FCSTD DOCUMENT  (FreeCAD 0.18R4 (GitTag))
Label: winding2
License: All rights reserved
LicenseURL: http://en.wikipedia.org/wiki/All_rights_reserved
objects: Sketcher::SketchObject×5, PartDesign::Body×2, Spreadsheet::Sheet×1
note: 7 computed .brp shape members not serialized (recipe doc carries the construction recipe); baked Part::Feature solids carry a one-line shape summary decoded from their .brp

FEATURE [Spreadsheet::Sheet] Spreadsheet  label="Variables"
  cells = A2=slotNumber; B2(slotNumber)=6; A3=outerDiameter; B3(outerDiameter)=50.15; A4=innerDiameter; B4(innerDiameter)=8; A5=stackLength; B5(stackLength)=26; A6=stackingFactor; B6(stackingFactor)=0.95; A7=cuttingThickness; B7(cuttingThickness)=0.1; A8=skewAngle; B8(skewAngle)=0; A9=segmentAngle; B9(segmentAngle)==360 / slotNumber; A10=tipHeightReduction; B10(tipHeightReduction)=50; A11=toothThickness; B11(toothThickness)=3; A12=yokeThickness; B12(yokeThickness)=2.8; A13=tipHeight; B13(tipHeight)=0.8; A14=tipAngle; B14(tipAngle)=95; A15=openingLeft; B15(openingLeft)=1; A16=openingRight; B16(openingRight)=1; A17=slotIsolation; B17(slotIsolation)=0.5; A18=windingAngle; B18(windingAngle)=35; A19=heightRatio; B19(heightRatio)=45; A20=roundingRadii; B20(roundingRadii)=0.2; A21=coilAxialHeight; B21(coilAxialHeight)=15
FEATURE [Sketcher::SketchObject] Sketch003  label="StatorSegment"
  MapMode = 5
  Support = -> [XY_Plane]
  expr: Constraints[71] = Variables.innerDiameter / 2
  expr: Constraints[26] = Variables.toothThickness / 2
  expr: Constraints[9] = Variables.segmentAngle
  expr: Constraints[27] = Variables.innerDiameter / 2 + Variables.yokeThickness
  expr: Constraints[35] = Variables.roundingRadii
  expr: Constraints[61] = Variables.tipHeight
  expr: Constraints[23] = Variables.tipAngle
  expr: Constraints[16] = Variables.tipHeight * (1 - Variables.tipHeightReduction / 100)
  expr: Constraints[12] = Variables.openingLeft
  expr: Constraints[72] = Variables.segmentAngle / 2
  expr: Constraints[5] = Variables.outerDiameter
  sketch-geometry (29):
    g0: ArcOfCircle [constr] CenterX=0 CenterY=0 CenterZ=0 NormalX=0 NormalY=0 NormalZ=1 AngleXU=0 Radius=25.075 StartAngle=-1.15e-14 EndAngle=1.0472
    g1: LineSegment [constr] StartX=0 StartY=0 StartZ=0 EndX=12.5375 EndY=21.7156 EndZ=0
    g2: LineSegment [constr] StartX=0 StartY=0 StartZ=0 EndX=25.075 EndY=-2.877e-13 EndZ=0
    g3: LineSegment [constr] StartX=0 StartY=0 StartZ=0 EndX=21.7156 EndY=12.5375 EndZ=0
    g4: LineSegment [constr] StartX=0.999801 StartY=25.0551 StartZ=0 EndX=21.1984 EndY=13.3934 EndZ=0
    g5: LineSegment [constr] StartX=21.1984 StartY=13.3934 StartZ=0 EndX=20.5958 EndY=13.0454 EndZ=0
    g6: LineSegment [constr] StartX=20.5056 StartY=12.9934 StartZ=0 EndX=20.852 EndY=13.1934 EndZ=0
    g7: ArcOfCircle CenterX=1.54226 CenterY=2.67128 CenterZ=0 NormalX=0 NormalY=0 NormalZ=1 AngleXU=0 Radius=21.9905 StartAngle=0.498928 EndAngle=1.0472
    g8: LineSegment StartX=20.4112 StartY=13.0374 StartZ=0 EndX=11.7908 EndY=17.0572 EndZ=0
    g9: LineSegment StartX=11.5331 StartY=16.9759 StartZ=0 EndX=4.84974 EndY=5.4 EndZ=0
    g10: LineSegment StartX=4.84974 StartY=5.2 StartZ=0 EndX=5.88897 EndY=3.4 EndZ=0
    g11: LineSegment [constr] StartX=4.84974 StartY=5.4 StartZ=0 EndX=3.5507 EndY=6.15 EndZ=0
    g12: LineSegment StartX=5.88897 StartY=3.4 StartZ=0 EndX=6.9282 EndY=1.6 EndZ=0
    g13: LineSegment StartX=7.10141 StartY=1.5 StartZ=0 EndX=20.4681 EndY=1.5 EndZ=0
    g14: LineSegment StartX=20.6673 StartY=1.68257 StartZ=0 EndX=21.4963 EndY=11.158 EndZ=0
    g15: LineSegment StartX=21.5956 StartY=11.3137 StartZ=0 EndX=21.8518 EndY=11.4617 EndZ=0
    g16: ArcOfCircle CenterX=3.08453 CenterY=2.65e-14 CenterZ=0 NormalX=0 NormalY=0 NormalZ=1 AngleXU=0 Radius=21.9905 StartAngle=-1.15e-14 EndAngle=0.548269
    g17: ArcOfCircle CenterX=21.6956 CenterY=11.1405 CenterZ=0 NormalX=0 NormalY=0 NormalZ=1 AngleXU=0 Radius=0.2 StartAngle=2.0944 EndAngle=3.05433
    g18: ArcOfCircle CenterX=20.4681 CenterY=1.7 CenterZ=0 NormalX=0 NormalY=0 NormalZ=1 AngleXU=0 Radius=0.2 StartAngle=4.71239 EndAngle=6.19592
    g19: ArcOfCircle CenterX=7.10141 CenterY=1.7 CenterZ=0 NormalX=0 NormalY=0 NormalZ=1 AngleXU=0 Radius=0.2 StartAngle=3.66519 EndAngle=4.71239
    g20: ArcOfCircle CenterX=11.7063 CenterY=16.8759 CenterZ=0 NormalX=0 NormalY=0 NormalZ=1 AngleXU=0 Radius=0.2 StartAngle=1.13446 EndAngle=2.61799
    g21: ArcOfCircle CenterX=20.4958 CenterY=13.2186 CenterZ=0 NormalX=0 NormalY=0 NormalZ=1 AngleXU=0 Radius=0.2 StartAngle=4.27606 EndAngle=5.23599
    g22: ArcOfCircle CenterX=5.02295 CenterY=5.3 CenterZ=0 NormalX=0 NormalY=0 NormalZ=1 AngleXU=0 Radius=0.2 StartAngle=2.61799 EndAngle=3.66519
    g23: LineSegment [constr] StartX=20.4112 StartY=13.0374 StartZ=0 EndX=20.5056 EndY=12.9934 EndZ=0
    g24: LineSegment [constr] StartX=20.5056 StartY=12.9934 StartZ=0 EndX=20.5958 EndY=13.0454 EndZ=0
    g25: LineSegment StartX=20.5958 StartY=13.0454 StartZ=0 EndX=20.852 EndY=13.1934 EndZ=0
    g26: LineSegment StartX=12.5375 StartY=21.7156 StartZ=0 EndX=2 EndY=3.4641 EndZ=0
    g27: LineSegment StartX=4 StartY=-4.59e-14 StartZ=0 EndX=25.075 EndY=-2.877e-13 EndZ=0
    g28: ArcOfCircle CenterX=0 CenterY=0 CenterZ=0 NormalX=0 NormalY=0 NormalZ=1 AngleXU=0 Radius=4 StartAngle=-1.15e-14 EndAngle=1.0472
  constraints (73):
    c: Coincident(g0,g-1)
    c: Coincident(g1,g0)
    c: Coincident(g1,g0)
    c: Coincident(g2,g0)
    c: Coincident(g2,g0)
    c: Diameter(g0) = 50.15
    c: Coincident(g3,g0)
    c: PointOnObject(g3,g0)
    c: Symmetric(g0,g0,g3)
    c: Angle(g2,g1) = 1.0472
    c: PointOnObject(g4,g0)
    c: Symmetric(g4,g4,g1)
    c: Distance(g4,g3) = 1
    c: Coincident(g5,g4)
    c: Parallel(g5,g3)
    c: PointOnObject(g6,g5)
    c: Distance(g6) = 0.4
    c: Coincident(g7,g0)
    c: Coincident(g7,g6)
    c: PointOnObject(g7,g1)
    c: PointOnObject(g10,g3)
    c: Perpendicular(g3,g10)
    c: Parallel(g1,g9)
    c: Angle(g9,g8) = 1.65806
    c: PointOnObject(g11,g1)
    c: Perpendicular(g1,g11)
    c: Distance(g11) = 1.5
    c: Distance(g-1,g10) = 6.8
    c: Coincident(g12,g10)
    c: Symmetric(g15,g7,g3)
    c: PointOnObject(g16,g2)
    c: Coincident(g16,g0)
    c: Coincident(g16,g15)
    c: Tangent(g14,g17) = 1.5708
    c: Tangent(g15,g17) = 1.5708
    c: Radius(g17) = 0.2
    c: Tangent(g13,g18) = -1.5708
    c: Tangent(g14,g18) = -1.5708
    c: Tangent(g12,g19) = -1.5708
    c: Tangent(g13,g19) = -1.5708
    c: Tangent(g8,g20) = -1.5708
    c: Tangent(g9,g20) = -1.5708
    c: Tangent(g5,g21) = 1.5708
    c: Tangent(g8,g21) = 1.5708
    c: Tangent(g10,g22) = -1.5708
    c: Tangent(g9,g22) = -1.5708
    c: Coincident(g11,g9)
    c: Equal(g17,g18)
    c: Equal(g19,g17)
    c: Equal(g22,g17)
    c: Equal(g20,g17)
    c: Symmetric(g13,g9,g3)
    c: Symmetric(g14,g8,g3)
    c: Symmetric(g14,g8,g3)
    c: Equal(g21,g17)
    c: Coincident(g23,g8)
    c: Coincident(g24,g23)
    c: Coincident(g24,g5)
    c: Parallel(g23,g8)
    c: Parallel(g24,g5)
    c: Coincident(g6,g23)
    c: Distance(g6,g4) = 0.8
    c: Coincident(g25,g21)
    c: Coincident(g25,g7)
    c: Coincident(g26,g7)
    c: PointOnObject(g26,g1)
    c: PointOnObject(g27,g2)
    c: Coincident(g27,g16)
    c: Coincident(g28,g-1)
    c: Coincident(g28,g26)
    c: Coincident(g28,g27)
    c: Radius(g28) = 4
    c: Angle(g-1,g3) = 0.523599
FEATURE [Sketcher::SketchObject] Sketch007  label="TerminalLeft"
  ExternalGeometry = -> [Sketch003]
  MapMode = 5
  Support = -> [XY_Plane]
  expr: Constraints[40] = Variables.slotIsolation / 2
  expr: Constraints[35] = Variables.windingAngle
  expr: Constraints[31] = 90
  expr: Constraints[21] = Variables.toothThickness / 2 + Variables.slotIsolation
  expr: Constraints[20] = Variables.innerDiameter / 2 + Variables.yokeThickness + Variables.slotIsolation
  expr: Constraints[5] = Variables.slotIsolation / sin(Variables.windingAngle)
  expr: Constraints[2] = (Variables.outerDiameter / 2 - Variables.innerDiameter / 2 - Variables.yokeThickness - Variables.tipHeight) * Variables.heightRatio / 100
  sketch-geometry (20):
    g0: LineSegment [constr] StartX=5.88897 StartY=3.4 StartZ=0 EndX=12.6992 EndY=7.33188 EndZ=0
    g1: LineSegment [constr] StartX=12.6992 StartY=7.33188 StartZ=0 EndX=12.2633 EndY=8.08681 EndZ=0
    g2: LineSegment [constr] StartX=19.8806 StartY=12.731 StartZ=0 EndX=11.8277 EndY=16.4862 EndZ=0
    g3: LineSegment [constr] StartX=11.8277 StartY=16.4862 StartZ=0 EndX=5.36936 EndY=5.3 EndZ=0
    g4: LineSegment [constr] StartX=5.36936 StartY=5.3 StartZ=0 EndX=7.27461 EndY=2 EndZ=0
    g5: LineSegment [constr] StartX=7.27461 StartY=2 StartZ=0 EndX=20.1913 EndY=2 EndZ=0
    g6: LineSegment [constr] StartX=20.1913 StartY=2 StartZ=0 EndX=20.9657 EndY=10.8516 EndZ=0
    g7: LineSegment [constr] StartX=20.9657 StartY=10.8516 StartZ=0 EndX=19.8806 EndY=12.731 EndZ=0
    g8: GeomPoint X=6.32199 Y=3.65 Z=0
    g9: LineSegment [constr] StartX=21.4963 StartY=11.158 StartZ=0 EndX=20.4112 EndY=13.0374 EndZ=0
    g10: LineSegment [constr] StartX=11.8277 StartY=16.4862 StartZ=0 EndX=11.3728 EndY=16.6983 EndZ=0
    g11: LineSegment [constr] StartX=11.8277 StartY=16.4862 StartZ=0 EndX=12.0398 EndY=16.941 EndZ=0
    g12: LineSegment [constr] StartX=7.8484 StartY=9.59383 StartZ=0 EndX=24.1334 EndY=2 EndZ=0
    g13: LineSegment [constr] StartX=7.97388 StartY=9.81116 StartZ=0 EndX=16.9541 EndY=5.6236 EndZ=0
    g14: LineSegment [constr] StartX=16.8485 StartY=5.39703 StartZ=0 EndX=16.9541 EndY=5.6236 EndZ=0
    g15: LineSegment [constr] StartX=16.9541 StartY=5.6236 StartZ=0 EndX=20.4112 EndY=13.0374 EndZ=0
    g16: LineSegment StartX=11.8277 StartY=16.4862 StartZ=0 EndX=20.1991 EndY=12.5825 EndZ=0
    g17: LineSegment StartX=20.1991 StartY=12.5825 StartZ=0 EndX=16.9541 EndY=5.6236 EndZ=0
    g18: LineSegment StartX=16.9541 StartY=5.6236 StartZ=0 EndX=7.97388 EndY=9.81116 EndZ=0
    g19: LineSegment StartX=7.97388 StartY=9.81116 StartZ=0 EndX=11.8277 EndY=16.4862 EndZ=0
  constraints (54):
    c: Coincident(g0,g-6)
    c: Perpendicular(g0,g-5)
    c: Distance(g0) = 7.86375
    c: Coincident(g1,g0)
    c: Parallel(g1,g-5)
    c: Distance(g1) = 0.871723
    c: Coincident(g2,g3)
    c: Coincident(g3,g4)
    c: Coincident(g4,g5)
    c: Horizontal(g5)
    c: Coincident(g5,g6)
    c: Coincident(g6,g7)
    c: Coincident(g7,g2)
    c: Parallel(g2,g-3)
    c: Parallel(g6,g-8)
    c: Parallel(g7,g4)
    c: Symmetric(g4,g3,g0)
    c: Symmetric(g5,g2,g0)
    c: PointOnObject(g8,g4)
    c: PointOnObject(g8,g0)
    c: Distance(g-1,g8) = 7.3
    c: DistanceY(g-1,g4) = 2
    c: Coincident(g9,g-8)
    c: Coincident(g9,g-3)
    c: Equal(g9,g7)
    c: Coincident(g10,g2)
    c: PointOnObject(g10,g-4)
    c: Coincident(g11,g2)
    c: PointOnObject(g11,g-3)
    c: Angle(g11,g10) = 1.5708
    c: Equal(g10,g11)
    c: Angle(g2,g11) = 1.5708
    c: PointOnObject(g12,g3)
    c: PointOnObject(g12,g5)
    c: PointOnObject(g0,g12)
    c: Angle(g4,g12) = 0.610865
    c: PointOnObject(g14,g12)
    c: PointOnObject(g13,g3)
    c: Coincident(g14,g13)
    c: Angle(g13,g14) = 1.5708
    c: Distance(g14) = 0.25
    c: Parallel(g12,g13)
    c: Coincident(g15,g13)
    c: Coincident(g15,g9)
    c: Parallel(g15,g14)
    c: Coincident(g16,g2)
    c: PointOnObject(g16,g15)
    c: Parallel(g16,g2)
    c: Coincident(g17,g16)
    c: Coincident(g17,g13)
    c: Coincident(g18,g17)
    c: Coincident(g18,g13)
    c: Coincident(g19,g18)
    c: Coincident(g19,g16)
FEATURE [Sketcher::SketchObject] Sketch008  label="TerminalRight"
  ExternalGeometry = -> [Sketch003]
  MapMode = 5
  Support = -> [XY_Plane]
  expr: Constraints[52] = Variables.slotIsolation / 2
  expr: Constraints[40] = Variables.slotIsolation / 2
  expr: Constraints[35] = Variables.windingAngle
  expr: Constraints[31] = 90
  expr: Constraints[21] = Variables.toothThickness / 2 + Variables.slotIsolation
  expr: Constraints[20] = Variables.innerDiameter / 2 + Variables.yokeThickness + Variables.slotIsolation
  expr: Constraints[5] = Variables.slotIsolation / sin(Variables.windingAngle)
  expr: Constraints[2] = (Variables.outerDiameter / 2 - Variables.innerDiameter / 2 - Variables.yokeThickness - Variables.tipHeight) * Variables.heightRatio / 100
  sketch-geometry (23):
    g0: LineSegment [constr] StartX=5.88897 StartY=3.4 StartZ=0 EndX=12.6992 EndY=7.33188 EndZ=0
    g1: LineSegment [constr] StartX=12.6992 StartY=7.33188 StartZ=0 EndX=12.2633 EndY=8.08681 EndZ=0
    g2: LineSegment [constr] StartX=19.8806 StartY=12.731 StartZ=0 EndX=11.8277 EndY=16.4862 EndZ=0
    g3: LineSegment [constr] StartX=11.8277 StartY=16.4862 StartZ=0 EndX=5.36936 EndY=5.3 EndZ=0
    g4: LineSegment [constr] StartX=5.36936 StartY=5.3 StartZ=0 EndX=7.27461 EndY=2 EndZ=0
    g5: LineSegment [constr] StartX=7.27461 StartY=2 StartZ=0 EndX=20.1913 EndY=2 EndZ=0
    g6: LineSegment [constr] StartX=20.1913 StartY=2 StartZ=0 EndX=20.9657 EndY=10.8516 EndZ=0
    g7: LineSegment [constr] StartX=20.9657 StartY=10.8516 StartZ=0 EndX=19.8806 EndY=12.731 EndZ=0
    g8: GeomPoint X=6.32199 Y=3.65 Z=0
    g9: LineSegment [constr] StartX=21.4963 StartY=11.158 StartZ=0 EndX=20.4112 EndY=13.0374 EndZ=0
    g10: LineSegment [constr] StartX=11.8277 StartY=16.4862 StartZ=0 EndX=11.3728 EndY=16.6983 EndZ=0
    g11: LineSegment [constr] StartX=11.8277 StartY=16.4862 StartZ=0 EndX=12.0398 EndY=16.941 EndZ=0
    g12: LineSegment [constr] StartX=7.8484 StartY=9.59383 StartZ=0 EndX=24.1334 EndY=2 EndZ=0
    g13: LineSegment [constr] StartX=7.97388 StartY=9.81116 StartZ=0 EndX=16.9541 EndY=5.6236 EndZ=0
    g14: LineSegment [constr] StartX=16.8485 StartY=5.39702 StartZ=0 EndX=16.9541 EndY=5.6236 EndZ=0
    g15: LineSegment [constr] StartX=16.9541 StartY=5.6236 StartZ=0 EndX=20.4112 EndY=13.0374 EndZ=0
    g16: LineSegment [constr] StartX=16.8485 StartY=5.39702 StartZ=0 EndX=15.2644 EndY=2 EndZ=0
    g17: LineSegment StartX=7.72292 StartY=9.3765 StartZ=0 EndX=16.7428 EndY=5.17045 EndZ=0
    g18: LineSegment [constr] StartX=16.7428 StartY=5.17045 StartZ=0 EndX=16.8485 EndY=5.39702 EndZ=0
    g19: LineSegment StartX=7.72292 StartY=9.3765 StartZ=0 EndX=5.36936 EndY=5.3 EndZ=0
    g20: LineSegment StartX=5.36936 StartY=5.3 StartZ=0 EndX=7.27461 EndY=2 EndZ=0
    g21: LineSegment StartX=7.27461 StartY=2 StartZ=0 EndX=15.2644 EndY=2 EndZ=0
    g22: LineSegment StartX=15.2644 StartY=2 StartZ=0 EndX=16.7428 EndY=5.17045 EndZ=0
  constraints (62):
    c: Coincident(g0,g-6)
    c: Perpendicular(g0,g-5)
    c: Distance(g0) = 7.86375
    c: Coincident(g1,g0)
    c: Parallel(g1,g-5)
    c: Distance(g1) = 0.871723
    c: Coincident(g2,g3)
    c: Coincident(g3,g4)
    c: Coincident(g4,g5)
    c: Horizontal(g5)
    c: Coincident(g5,g6)
    c: Coincident(g6,g7)
    c: Coincident(g7,g2)
    c: Parallel(g2,g-3)
    c: Parallel(g6,g-8)
    c: Parallel(g7,g4)
    c: Symmetric(g4,g3,g0)
    c: Symmetric(g5,g2,g0)
    c: PointOnObject(g8,g4)
    c: PointOnObject(g8,g0)
    c: Distance(g-1,g8) = 7.3
    c: DistanceY(g-1,g4) = 2
    c: Coincident(g9,g-8)
    c: Coincident(g9,g-3)
    c: Equal(g9,g7)
    c: Coincident(g10,g2)
    c: PointOnObject(g10,g-4)
    c: Coincident(g11,g2)
    c: PointOnObject(g11,g-3)
    c: Angle(g11,g10) = 1.5708
    c: Equal(g10,g11)
    c: Angle(g2,g11) = 1.5708
    c: PointOnObject(g12,g3)
    c: PointOnObject(g12,g5)
    c: PointOnObject(g0,g12)
    c: Angle(g4,g12) = 0.610865
    c: PointOnObject(g14,g12)
    c: PointOnObject(g13,g3)
    c: Coincident(g14,g13)
    c: Angle(g13,g14) = 1.5708
    c: Distance(g14) = 0.25
    c: Parallel(g12,g13)
    c: Coincident(g15,g13)
    c: Coincident(g15,g9)
    c: Parallel(g15,g14)
    c: Coincident(g16,g14)
    c: PointOnObject(g16,g5)
    c: Parallel(g16,g15)
    c: PointOnObject(g17,g3)
    c: PointOnObject(g17,g16)
    c: Coincident(g18,g17)
    c: Coincident(g18,g14)
    c: Distance(g18) = 0.25
    c: Angle(g18,g17) = 1.5708
    c: Coincident(g19,g17)
    c: Coincident(g19,g3)
    c: Coincident(g20,g19)
    c: Coincident(g20,g4)
    c: Coincident(g21,g20)
    c: Coincident(g21,g16)
    c: Coincident(g22,g21)
    c: Coincident(g22,g17)
FEATURE [PartDesign::Body] Body  label="TopView"
  Group = -> [Sketch003,Sketch007,Sketch008]
  Origin = -> Origin
FEATURE [Sketcher::SketchObject] Sketch  label="StatorSde"
  MapMode = 5
  Support = -> [XY_Plane001]
  expr: Constraints[20] = Variables.stackLength
  expr: Constraints[17] = Variables.innerDiameter
  expr: Constraints[16] = Variables.outerDiameter
  sketch-geometry (8):
    g0: LineSegment StartX=-13 StartY=25.075 StartZ=0 EndX=13 EndY=25.075 EndZ=0
    g1: LineSegment StartX=13 StartY=25.075 StartZ=0 EndX=13 EndY=4 EndZ=0
    g2: LineSegment StartX=13 StartY=4 StartZ=0 EndX=-13 EndY=4 EndZ=0
    g3: LineSegment StartX=-13 StartY=4 StartZ=0 EndX=-13 EndY=25.075 EndZ=0
    g4: LineSegment StartX=-13 StartY=-4 StartZ=0 EndX=13 EndY=-4 EndZ=0
    g5: LineSegment StartX=13 StartY=-4 StartZ=0 EndX=13 EndY=-25.075 EndZ=0
    g6: LineSegment StartX=13 StartY=-25.075 StartZ=0 EndX=-13 EndY=-25.075 EndZ=0
    g7: LineSegment StartX=-13 StartY=-25.075 StartZ=0 EndX=-13 EndY=-4 EndZ=0
  constraints (21):
    c: Coincident(g0,g1)
    c: Coincident(g1,g2)
    c: Coincident(g2,g3)
    c: Coincident(g3,g0)
    c: Horizontal(g0)
    c: Vertical(g1)
    c: Vertical(g3)
    c: Coincident(g4,g5)
    c: Coincident(g5,g6)
    c: Coincident(g6,g7)
    c: Coincident(g7,g4)
    c: Horizontal(g6)
    c: Vertical(g5)
    c: Vertical(g7)
    c: Symmetric(g2,g1,g-2)
    c: Symmetric(g4,g4,g-2)
    c: DistanceY(g6,g0) = 50.15
    c: DistanceY(g4,g2) = 8
    c: Symmetric(g4,g2,g-1)
    c: Equal(g7,g3)
    c: DistanceX(g6,g6) = 26
FEATURE [Sketcher::SketchObject] Sketch009  label="WindingSide"
  ExternalGeometry = -> [Sketch]
  MapMode = 5
  Support = -> [XY_Plane001]
  expr: Constraints[18] = Variables.coilAxialHeight
  expr: Constraints[8] = Variables.coilAxialHeight
  sketch-geometry (12):
    g0: ArcOfEllipse CenterX=-13 CenterY=0 CenterZ=0 NormalX=0 NormalY=0 NormalZ=1 MajorRadius=25.075 MinorRadius=15 AngleXU=1.5708 StartAngle=1e-16 EndAngle=3.14159
    g1: LineSegment [constr] StartX=-13 StartY=25.075 StartZ=0 EndX=-13 EndY=-25.075 EndZ=0
    g2: LineSegment [constr] StartX=-28 StartY=0 StartZ=0 EndX=2 EndY=0 EndZ=0
    g3: GeomPoint X=-13 Y=20.0937 Z=0
    g4: GeomPoint X=-13 Y=-20.0937 Z=0
    g5: LineSegment StartX=-13 StartY=25.075 StartZ=0 EndX=-13 EndY=-25.075 EndZ=0
    g6: ArcOfEllipse CenterX=13 CenterY=0 CenterZ=0 NormalX=0 NormalY=0 NormalZ=1 MajorRadius=25.075 MinorRadius=15 AngleXU=-1.5708 StartAngle=-9.8e-15 EndAngle=3.14159
    g7: LineSegment [constr] StartX=13 StartY=-25.075 StartZ=0 EndX=13 EndY=25.075 EndZ=0
    g8: LineSegment [constr] StartX=28 StartY=0 StartZ=0 EndX=-2 EndY=0 EndZ=0
    g9: GeomPoint X=13 Y=-20.0937 Z=0
    g10: GeomPoint X=13 Y=20.0937 Z=0
    g11: LineSegment StartX=13 StartY=25.075 StartZ=0 EndX=13 EndY=-25.075 EndZ=0
  constraints (18):
    c: InternalAlignment(g1-g4 -> g0) x4
    c: PointOnObject(g0,g-4)
    c: Horizontal(g2)
    c: PointOnObject(g0,g-1)
    c: PointOnObject(g1,g-3)
    c: DistanceX(g2,g0) = 15
    c: Coincident(g0,g-3)
    c: Coincident(g5,g0)
    c: Coincident(g5,g0)
    c: InternalAlignment(g7-g10 -> g6) x4
    c: PointOnObject(g6,g-1)
    c: Coincident(g6,g-6)
    c: DistanceX(g6,g8) = 15
    c: Coincident(g6,g7)
    c: Horizontal(g8)
    c: PointOnObject(g6,g7)
    c: Coincident(g11,g6)
    c: Coincident(g11,g6)
FEATURE [PartDesign::Body] Body001  label="SideView"
  Group = -> [Sketch,Sketch009]
  Origin = -> Origin001
